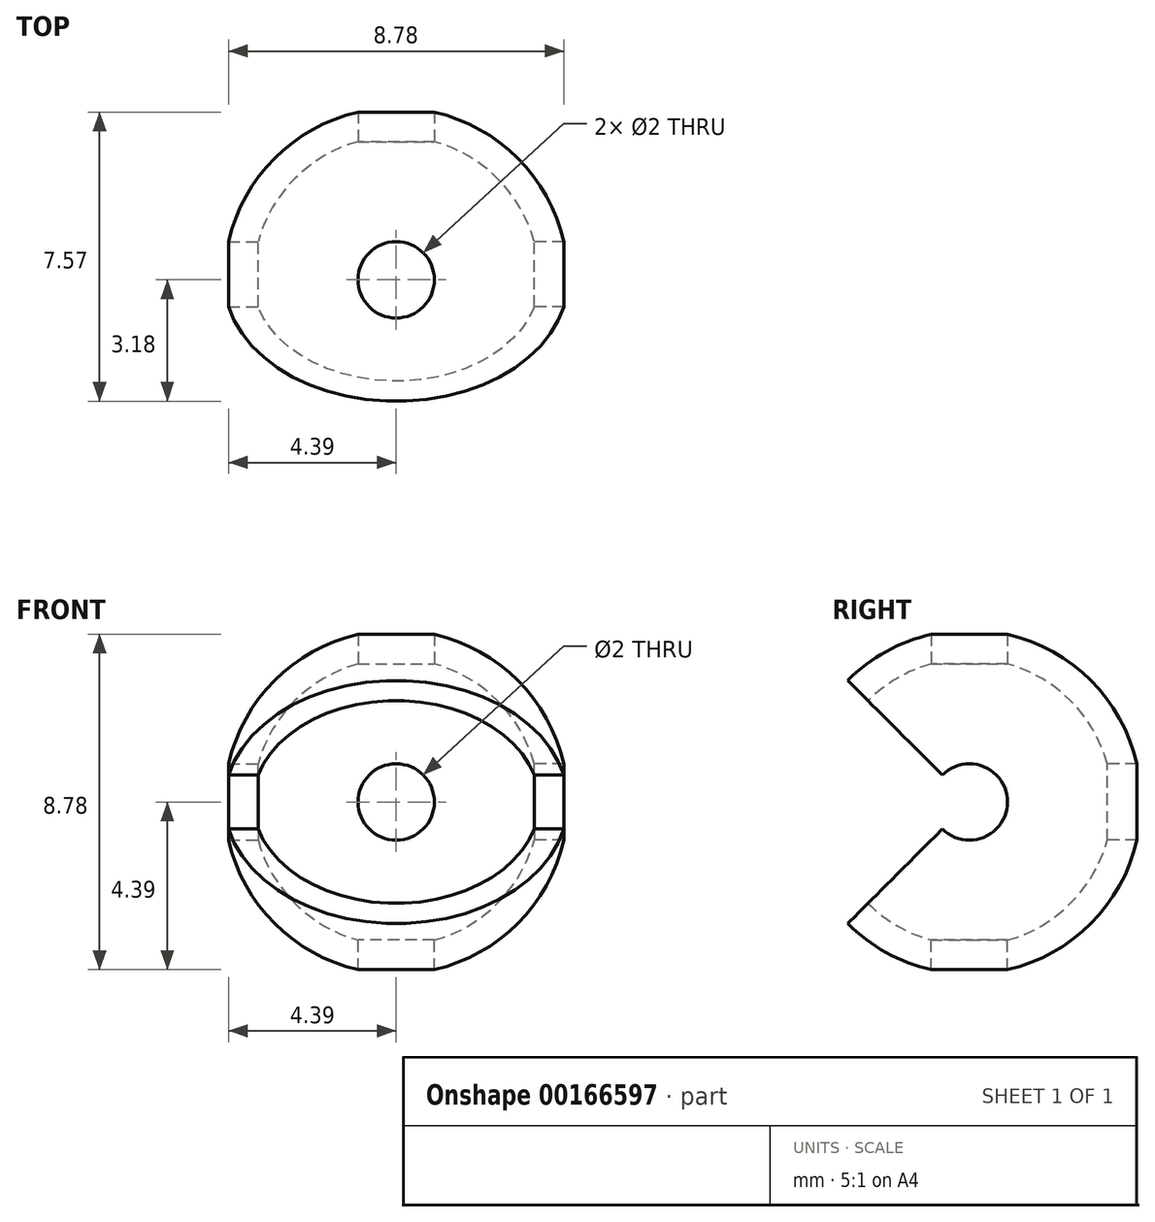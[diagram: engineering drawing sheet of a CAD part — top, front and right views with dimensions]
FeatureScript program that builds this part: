
annotation { "Feature Type Name" : "Feature", "Feature Type Description" : "" }
export const myFeature = defineFeature(function(context is Context, id is Id, definition is map)
    precondition{}
    {
        {
            var Q0;
            Q0=qCreatedBy(makeId("Top.planeOp"),FACE);
            var sketch = newSketch(context, id + "F0", { "sketchPlane" : qUnion([Q0])});
            skLineSegment(sketch, "E0", {"start": v(-5.3, 0) * mm, "end": v(5.63, 0) * mm});
            skArc(sketch, "E1", {"start": v(4.5, 0) * mm, "mid": v(0, 4.5) * mm, "end": v(-4.5, 0) * mm});
            skSolve(sketch);
        }
        {
            var Q0;
            {var subQ0=sQuery(id+"F0.wireOp",EDGE,"E1");Q0=makeQuery(id+"F0.imprint","IMPRINT",FACE,{"disambiguationData":[TD([[makeQuery(id+"F0.imprint","IMPRINT",EDGE,{"derivedFrom":subQ0}),1.0]])]});}
            var Q1;
            Q1=sQuery(id+"F0.wireOp",EDGE,"E0");
            revolve(context, id + "F1", {"entities" : qUnion([Q0]), "axis" : qUnion([Q1]), "revolveType" : RevolveType.ONE_DIRECTION, "angle" : 270 * degree});
        }
        {
            var Q0;
            Q0=makeQuery(id+"F1.opRevolve","CAP_FACE",FACE,{"disambiguationData":[OSD([sQuery(id+"F0.wireOp",EDGE,"E0"),sQuery(id+"F0.wireOp",EDGE,"E1")])],"isStart":true});
            var Q1;
            Q1=makeQuery(id+"F1.opRevolve","CAP_FACE",FACE,{"disambiguationData":[OSD([sQuery(id+"F0.wireOp",EDGE,"E0"),sQuery(id+"F0.wireOp",EDGE,"E1")])],"isStart":false});
            var Q2;
            Q2=makeQuery(id+"F1.opRevolve","SWEPT_BODY",BODY,{"disambiguationData":[OSD([sQuery(id+"F0.wireOp",EDGE,"E0"),sQuery(id+"F0.wireOp",EDGE,"E1")])]});
            shell(context, id + "F14", {"entities" : qUnion([Q0, Q1]), "parts" : qUnion([Q2]), "thickness" : .75 * mm});
        }
        {
            var Q0;
            Q0=qCreatedBy(makeId("Right.planeOp"),FACE);
            var sketch = newSketch(context, id + "F2", { "sketchPlane" : qUnion([Q0])});
            skPoint(sketch, "E2", {"position": v(0, 0) * mm});
            skSolve(sketch);
        }
        {
            var Q0;
            Q0=sQuery(id+"F2.wireOp",VERTEX,"E2");
            var Q1;
            Q1=makeQuery(id+"F1.opRevolve","SWEPT_BODY",BODY,{"disambiguationData":[OSD([sQuery(id+"F0.wireOp",EDGE,"E0"),sQuery(id+"F0.wireOp",EDGE,"E1")])]});
            hole(context, id + "F3", {"style" : HoleStyle.SIMPLE, "endStyle" : HoleEndStyle.THROUGH, "holeDiameter" : 2 * mm, "locations" : qUnion([Q0]), "scope" : qUnion([Q1]), "isTappedThrough" : true});
        }
        {
            var Q0;
            Q0=qCreatedBy(makeId("Right.planeOp"),FACE);
            var sketch = newSketch(context, id + "F4", { "sketchPlane" : qUnion([Q0])});
            skPoint(sketch, "E3", {"position": v(0, 0) * mm});
            skSolve(sketch);
        }
        {
            var Q0;
            Q0=sQuery(id+"F4.wireOp",VERTEX,"E3");
            var Q1;
            Q1=makeQuery(id+"F1.opRevolve","SWEPT_BODY",BODY,{"disambiguationData":[OSD([sQuery(id+"F0.wireOp",EDGE,"E0"),sQuery(id+"F0.wireOp",EDGE,"E1")])]});
            hole(context, id + "F5", {"style" : HoleStyle.SIMPLE, "endStyle" : HoleEndStyle.THROUGH, "oppositeDirection" : true, "holeDiameter" : 2 * mm, "locations" : qUnion([Q0]), "scope" : qUnion([Q1]), "isTappedThrough" : true});
        }
        {
            var Q0;
            Q0=qCreatedBy(makeId("Top.planeOp"),FACE);
            var sketch = newSketch(context, id + "F6", { "sketchPlane" : qUnion([Q0])});
            skLineSegment(sketch, "E4", {"start": v(20, 0) * mm, "end": v(-20, 0) * mm});
            skPoint(sketch, "E5", {"position": v(4, 1) * mm});
            skPoint(sketch, "E6", {"position": v(-4, 1) * mm});
            skPoint(sketch, "E7", {"position": v(0, 0) * mm});
            skSolve(sketch);
        }
        {
            var Q0;
            Q0=makeQuery(id+"F1.opRevolve","SWEPT_BODY",BODY,{"disambiguationData":[OSD([sQuery(id+"F0.wireOp",EDGE,"E0"),sQuery(id+"F0.wireOp",EDGE,"E1")])]});
            var Q1;
            Q1=sQuery(id+"F6.wireOp",EDGE,"E4");
            var Q2;
            Q2=sQuery(id+"F6.wireOp",EDGE,"E4");
            transform(context, id + "F7", {"entities" : qUnion([Q0]), "transformType" : TransformType.ROTATION, "transformAxis" : qUnion([Q2]), "angle" : 135 * degree, "makeCopy" : false});
        }
        {
            var Q0;
            Q0=qCreatedBy(makeId("Front.planeOp"),FACE);
            var sketch = newSketch(context, id + "F8", { "sketchPlane" : qUnion([Q0])});
            skPoint(sketch, "E8", {"position": v(0, 0) * mm});
            skSolve(sketch);
        }
        {
            var Q0;
            Q0=sQuery(id+"F8.wireOp",VERTEX,"E8");
            var Q1;
            Q1=makeQuery(id+"F1.opRevolve","SWEPT_BODY",BODY,{"disambiguationData":[OSD([sQuery(id+"F0.wireOp",EDGE,"E0"),sQuery(id+"F0.wireOp",EDGE,"E1")])]});
            hole(context, id + "F9", {"style" : HoleStyle.SIMPLE, "endStyle" : HoleEndStyle.THROUGH, "holeDiameter" : 2 * mm, "locations" : qUnion([Q0]), "scope" : qUnion([Q1]), "isTappedThrough" : true});
        }
        {
            var Q0;
            Q0=qCreatedBy(makeId("Top.planeOp"),FACE);
            var sketch = newSketch(context, id + "F10", { "sketchPlane" : qUnion([Q0])});
            skPoint(sketch, "E9", {"position": v(0, 0) * mm});
            skSolve(sketch);
        }
        {
            var Q0;
            Q0=sQuery(id+"F10.wireOp",VERTEX,"E9");
            var Q1;
            Q1=makeQuery(id+"F1.opRevolve","SWEPT_BODY",BODY,{"disambiguationData":[OSD([sQuery(id+"F0.wireOp",EDGE,"E0"),sQuery(id+"F0.wireOp",EDGE,"E1")])]});
            hole(context, id + "F11", {"style" : HoleStyle.SIMPLE, "endStyle" : HoleEndStyle.THROUGH, "holeDiameter" : 2 * mm, "locations" : qUnion([Q0]), "scope" : qUnion([Q1]), "isTappedThrough" : true});
        }
        {
            var Q0;
            Q0=qCreatedBy(makeId("Top.planeOp"),FACE);
            var sketch = newSketch(context, id + "F12", { "sketchPlane" : qUnion([Q0])});
            skPoint(sketch, "E10", {"position": v(0, 0) * mm});
            skSolve(sketch);
        }
        {
            var Q0;
            Q0=sQuery(id+"F12.wireOp",VERTEX,"E10");
            var Q1;
            Q1=makeQuery(id+"F1.opRevolve","SWEPT_BODY",BODY,{"disambiguationData":[OSD([sQuery(id+"F0.wireOp",EDGE,"E0"),sQuery(id+"F0.wireOp",EDGE,"E1")])]});
            hole(context, id + "F13", {"style" : HoleStyle.SIMPLE, "endStyle" : HoleEndStyle.THROUGH, "oppositeDirection" : true, "holeDiameter" : 2 * mm, "locations" : qUnion([Q0]), "scope" : qUnion([Q1]), "isTappedThrough" : true});
        }
    });
